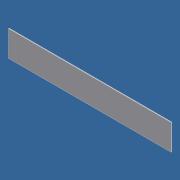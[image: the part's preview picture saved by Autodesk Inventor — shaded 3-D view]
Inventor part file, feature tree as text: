
AUTODESK INVENTOR PART (.ipt)
format: ipt  version: 2012 (Build 160160000, 160)  size: 64,000 bytes
history: native  units: in
note: dims shown in document units (in); Inventor stores cm internally (conversion verified against a paired STEP export)
features: extrude x1, sketch x1
ambient origin geometry x8: Origin, YZ Plane, XZ Plane, XY Plane, X Axis, Y Axis, Z Axis, Center Point
bodies: Solid1 (feature_tree)
feature tree (2):
  extrude  "Extrusion1"  Depth=50.5in
  sketch  "Sketch1"  dims[d0=8.0in d1=50.5in d2=0.25in d3=0.0in]
